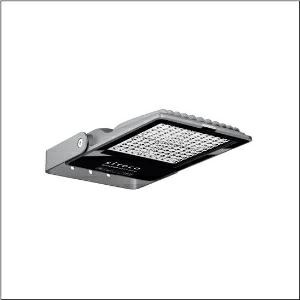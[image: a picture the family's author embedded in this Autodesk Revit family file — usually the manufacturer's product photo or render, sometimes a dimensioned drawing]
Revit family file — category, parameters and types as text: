
# Revit family: sicompact_r__31_mini___pl32_5xa7571f1k23_4385
name_source: partatom
category: Lighting Fixtures
units: mm (PartAtom-declared; Revit-internal decimal feet)

## family parameters
Cut with Voids When Loaded = No
Host = Face
Light Source = No
Part Type = Normal
Room Calculation Point = No
Round Connector Dimension = Use Diameter
Shared = No

## types (1)
- SiCompact® 31 mini  PL32 (1 x LED, 20000 lm, 130 W, 3000K)
    Apparent Load = 130 VA
    CIE Flux Codes = 32 69 98 100 100
    Color Rendering = 70
    Color Temperature = 3000K
    Default Elevation = 1800 mm
    Description = SiCompact® 31 mini, floodlight, primary light control with lens, of plastic, of toughened safety glass, transparent, light distribution: PL32, light emission: direct distribution, primary light characteristic: asymmetric, installation type: surface-mounted, LED, High Power LED, rated luminous flux: 20.000lm, luminous efficacy: 154lm/W, light colour: 730, colour temperature: 3000K, control gear: ECG, with cable, 3x 1.5mm², mains connection: 220..240V, AC, 50/60Hz, connection cable pre-assembled, cable length: 2m, rated input power: 130W, of diecast aluminium, specular, metallic grey (RAL 9006), length: 461mm, width: 261mm, height: 62mm, bracket, of sheet steel, coated, metallic grey (RAL 9006), ON/OFF, protection rating (complete): IP66, insulation class (complete): insulation class I (protective earthing), certification: CE, ENEC, impact resistance: IK08, permissible operating ambient temperature: -40..+45°C, packaging unit: 1 piece

Light Distribution: PL32
    Height = 62 mm  [stored 0.203412 ft]
    Lamp = 1 x LED
    Lamp Light Flux = 20000 lm
    Lamp Power = 130 W
    Lamp count = 1
    Length = 460 mm
    Luminous efficacy = 154 lm/W
    Manufacturer = Siteco
    ModVariant = No
    Model = 5XA7571F1K23
    Mounting Place = Wall
    Mounting Type = Surface mounted
    Number of Poles = 1
    OnlyDefault = Yes
    Power Factor = 1
    Product Name = SiCompact® 31 mini | PL32
    Product group = floodlight | wall mounted
    ProductGroupID = 2001
    Protection Class = Protection class I
    Protection Degree = IP 66
    RLX_Detail_Level = 1
    RLX_Emergency_Light_Flux = 0 lm
    RLX_Emergency_Type = 0
    RLX_Emergency_Type_DB = No
    RlxData = <blob elided: 126697 chars, md5=56bdba2d>
    Socket = socket
    Standby Power = 0 W
    System Light Flux = 20000 lm
    System Power = 130 W
    Type Comments = Product without accessories
    Type Image = l_1006951.jpg
    URL = http://relux.com
    VarID = ---
    Voltage = 0 V
    Weight = 0.00 kg
    Width = 260 mm

note: [stored X ft] marks values corroborated as IEEE doubles in the binary element streams (Revit-internal decimal feet)

## geometry (parser evidence)
native form markers: Blend x4, Sweep x12
no freeform markers — native parametric forms only
